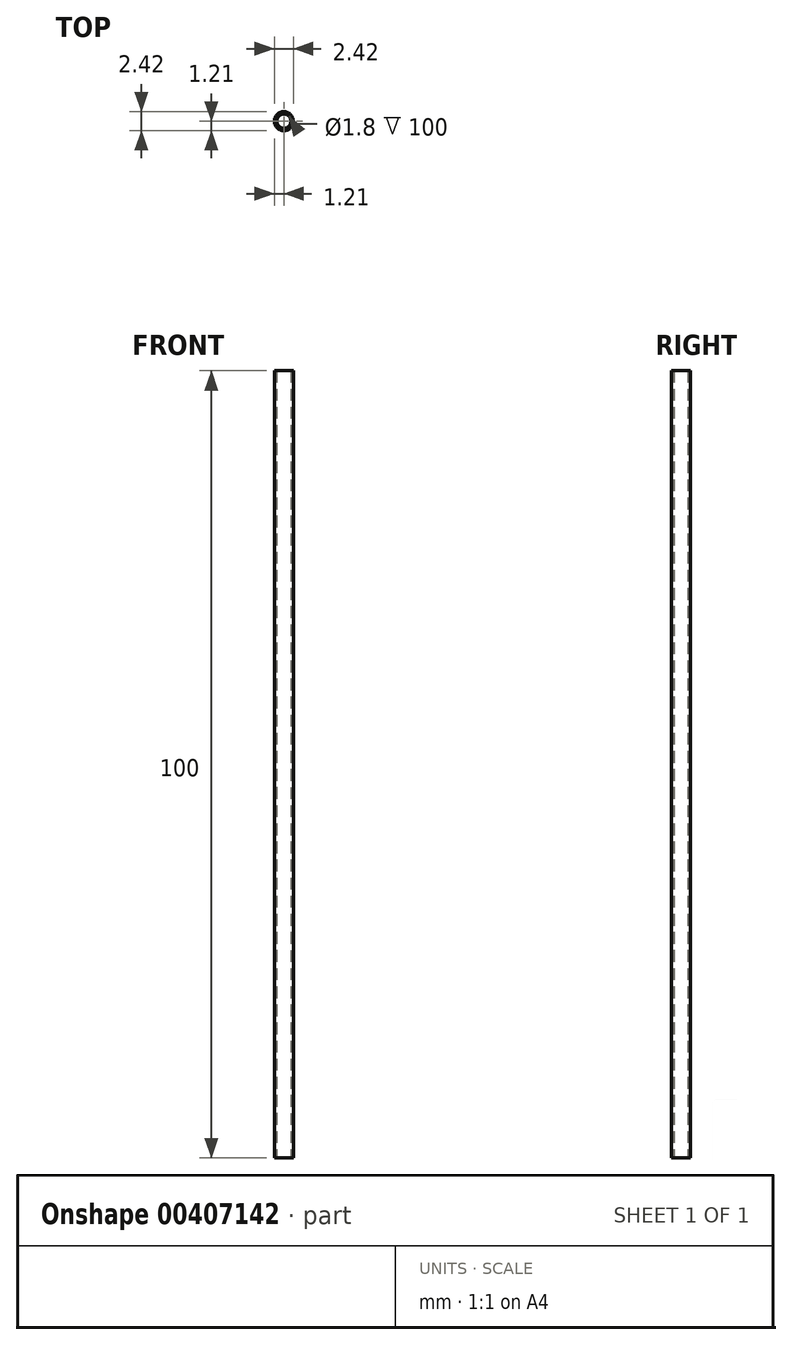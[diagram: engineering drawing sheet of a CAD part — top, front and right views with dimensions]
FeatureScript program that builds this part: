
annotation { "Feature Type Name" : "Feature", "Feature Type Description" : "" }
export const myFeature = defineFeature(function(context is Context, id is Id, definition is map)
    precondition{}
    {
        {
            var Q0;
            Q0=qCreatedBy(makeId("Top.planeOp"),FACE);
            var sketch = newSketch(context, id + "F0", { "sketchPlane" : qUnion([Q0])});
            skCircle(sketch, "E0", {"center": v(0, 0) * mm, "radius": 1.2 * mm});
            skCircle(sketch, "E1", {"center": v(0, 0) * mm, "radius": 0.9 * mm});
            skSolve(sketch);
        }
        {
            var Q0;
            Q0 = qSketchRegion(id + "F0", true);
            extrude(context, id + "F1", {"entities" : qUnion([Q0]), "depth" : 100 * mm});
        }
    });
